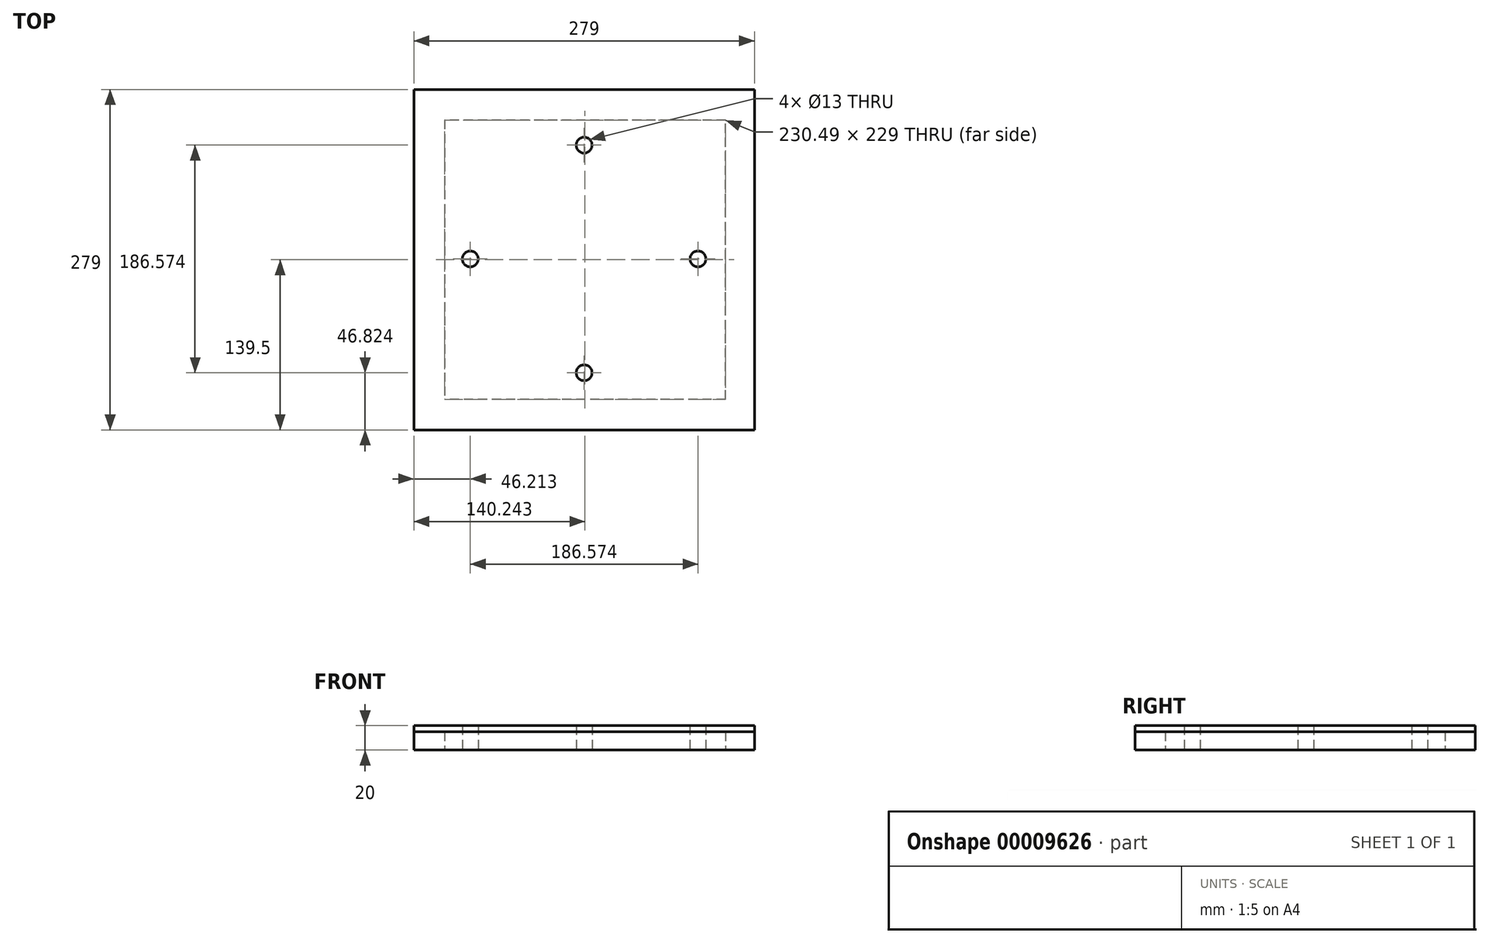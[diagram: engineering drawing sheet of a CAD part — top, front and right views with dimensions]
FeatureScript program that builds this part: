
annotation { "Feature Type Name" : "Feature", "Feature Type Description" : "" }
export const myFeature = defineFeature(function(context is Context, id is Id, definition is map)
    precondition{}
    {
        {
            var Q0;
            Q0=qCreatedBy(makeId("Top.planeOp"),FACE);
            var sketch = newSketch(context, id + "F0", { "sketchPlane" : qUnion([Q0])});
            skLineSegment(sketch, "E0.rect.bottom", {"start": v(89.5, 89.5) * mm, "end": v(-89.5, 89.5) * mm});
            skLineSegment(sketch, "E0.rect.top", {"start": v(89.5, -89.5) * mm, "end": v(-89.5, -89.5) * mm});
            skLineSegment(sketch, "E0.rect.left", {"start": v(89.5, 89.5) * mm, "end": v(89.5, -89.5) * mm});
            skLineSegment(sketch, "E0.rect.right", {"start": v(-89.5, 89.5) * mm, "end": v(-89.5, -89.5) * mm});
            skPoint(sketch, "E0.rect.middle", {"position": v(0, 0) * mm});
            skLineSegment(sketch, "E1.0", {"start": v(115.99, 114.5) * mm, "end": v(-114.5, 114.5) * mm});
            skLineSegment(sketch, "E1.2", {"start": v(115.99, -114.5) * mm, "end": v(-114.5, -114.5) * mm});
            skLineSegment(sketch, "E1.3", {"start": v(-114.5, 114.5) * mm, "end": v(-114.5, -114.5) * mm});
            skLineSegment(sketch, "E2.0", {"start": v(139.5, 139.5) * mm, "end": v(-139.5, 139.5) * mm});
            skLineSegment(sketch, "E2.1", {"start": v(139.5, 139.5) * mm, "end": v(139.5, -139.5) * mm});
            skLineSegment(sketch, "E2.2", {"start": v(139.5, -139.5) * mm, "end": v(-139.5, -139.5) * mm});
            skLineSegment(sketch, "E2.3", {"start": v(-139.5, 139.5) * mm, "end": v(-139.5, -139.5) * mm});
            skLineSegment(sketch, "E3", {"start": v(-3.54, 111.58) * mm, "end": v(-110.96, 4.15) * mm});
            skLineSegment(sketch, "E4", {"start": v(-110.96, -2.92) * mm, "end": v(-3.54, -110.35) * mm});
            skLineSegment(sketch, "E5", {"start": v(3.54, -110.35) * mm, "end": v(110.96, -2.92) * mm});
            skLineSegment(sketch, "E6", {"start": v(110.96, 4.15) * mm, "end": v(3.54, 111.58) * mm});
            skLineSegment(sketch, "E7", {"start": v(57.25, 57.86) * mm, "end": v(-57.25, -56.64) * mm, "construction": true});
            skLineSegment(sketch, "E8", {"start": v(-57.25, 57.86) * mm, "end": v(57.25, -56.64) * mm, "construction": true});
            skPoint(sketch, "E9.visualSharp", {"position": v(0, 115.11) * mm});
            skArc(sketch, "E9.filletArc", {"start": v(3.54, 111.58) * mm, "mid": v(0, 113.04) * mm, "end": v(-3.54, 111.58) * mm});
            skPoint(sketch, "E10.visualSharp", {"position": v(114.5, 0.61) * mm});
            skArc(sketch, "E10.filletArc", {"start": v(110.96, -2.92) * mm, "mid": v(112.43, 0.61) * mm, "end": v(110.96, 4.15) * mm});
            skPoint(sketch, "E11.visualSharp", {"position": v(0, -113.89) * mm});
            skArc(sketch, "E11.filletArc", {"start": v(-3.54, -110.35) * mm, "mid": v(0, -111.82) * mm, "end": v(3.54, -110.35) * mm});
            skPoint(sketch, "E12.visualSharp", {"position": v(-114.5, 0.61) * mm});
            skArc(sketch, "E12.filletArc", {"start": v(-110.96, 4.15) * mm, "mid": v(-112.43, 0.61) * mm, "end": v(-110.96, -2.92) * mm});
            skLineSegment(sketch, "E13", {"start": v(-57.25, 57.86) * mm, "end": v(57.25, 57.86) * mm});
            skLineSegment(sketch, "E14", {"start": v(57.25, 57.86) * mm, "end": v(57.25, -56.64) * mm});
            skLineSegment(sketch, "E15", {"start": v(57.25, -56.64) * mm, "end": v(-57.25, -56.64) * mm});
            skLineSegment(sketch, "E16", {"start": v(-57.25, -56.64) * mm, "end": v(-57.25, 57.86) * mm});
            skLineSegment(sketch, "E17", {"start": v(0, 0) * mm, "end": v(0, -113.89) * mm, "construction": true});
            skPoint(sketch, "E18", {"position": v(0, -92.68) * mm});
            skLineSegment(sketch, "E19", {"start": v(-107.43, 0.61) * mm, "end": v(107.43, 0.61) * mm, "construction": true});
            skLineSegment(sketch, "E20", {"start": v(0, 108.04) * mm, "end": v(0, 0) * mm, "construction": true});
            skPoint(sketch, "E21", {"position": v(-93.29, 0.61) * mm});
            skPoint(sketch, "E22", {"position": v(0, 93.9) * mm});
            skPoint(sketch, "E23", {"position": v(93.29, 0.61) * mm});
            skCircle(sketch, "E24", {"center": v(0, -92.68) * mm, "radius": 6.5 * mm});
            skCircle(sketch, "E25", {"center": v(93.29, 0.61) * mm, "radius": 6.5 * mm});
            skCircle(sketch, "E26", {"center": v(-93.29, 0.61) * mm, "radius": 6.5 * mm});
            skCircle(sketch, "E27", {"center": v(0, 93.9) * mm, "radius": 6.5 * mm});
            skLineSegment(sketch, "E28", {"start": v(115.99, -114.5) * mm, "end": v(115.99, 114.5) * mm});
            skPoint(sketch, "E29.orphan", {"position": v(109.2, 114.5) * mm});
            skSolve(sketch);
        }
        {
            var Q0;
            Q0=makeQuery(id+"F0.imprint","IMPRINT",FACE,{"disambiguationData":[TD([[makeQuery(id+"F0.imprint","IMPRINT",EDGE,{"derivedFrom":sQuery(id+"F0.wireOp",EDGE,"E0.rect.bottom")}),1.0]])]});
            var Q1;
            Q1=makeQuery(id+"F0.imprint","IMPRINT",FACE,{"disambiguationData":[TD([[makeQuery(id+"F0.imprint","IMPRINT",EDGE,{"derivedFrom":sQuery(id+"F0.wireOp",EDGE,"E13")}),-1.0]])]});
            var Q2;
            {var subQ1=sQuery(id+"F0.wireOp",EDGE,"E0.rect.right");var subQ4=sQuery(id+"F0.wireOp",EDGE,"E0.rect.bottom");var subQ6=makeQuery(id+"F0.imprint","INTERSECT",VERTEX,{"derivedFrom":[subQ4,subQ1]});Q2=makeQuery(id+"F0.imprint","IMPRINT",FACE,{"disambiguationData":[TD([[makeQuery(id+"F0.imprint","IMPRINT",EDGE,{"disambiguationData":[TD([[subQ6,1.0]])],"derivedFrom":subQ4}),1.0]])]});}
            var Q3;
            {var subQ4=sQuery(id+"F0.wireOp",EDGE,"E16");Q3=makeQuery(id+"F0.imprint","IMPRINT",FACE,{"disambiguationData":[TD([[makeQuery(id+"F0.imprint","IMPRINT",EDGE,{"derivedFrom":subQ4}),1.0]])]});}
            var Q4;
            {var subQ1=sQuery(id+"F0.wireOp",EDGE,"E0.rect.bottom");var subQ4=sQuery(id+"F0.wireOp",EDGE,"E0.rect.left");var subQ6=makeQuery(id+"F0.imprint","INTERSECT",VERTEX,{"derivedFrom":[subQ1,subQ4]});Q4=makeQuery(id+"F0.imprint","IMPRINT",FACE,{"disambiguationData":[TD([[makeQuery(id+"F0.imprint","IMPRINT",EDGE,{"disambiguationData":[TD([[subQ6,-1.0]])],"derivedFrom":subQ1}),1.0]])]});}
            var Q5;
            {var subQ4=sQuery(id+"F0.wireOp",EDGE,"E14");Q5=makeQuery(id+"F0.imprint","IMPRINT",FACE,{"disambiguationData":[TD([[makeQuery(id+"F0.imprint","IMPRINT",EDGE,{"derivedFrom":subQ4}),1.0]])]});}
            var Q6;
            {var subQ1=sQuery(id+"F0.wireOp",EDGE,"E0.rect.left");var subQ4=sQuery(id+"F0.wireOp",EDGE,"E0.rect.top");var subQ6=makeQuery(id+"F0.imprint","INTERSECT",VERTEX,{"derivedFrom":[subQ4,subQ1]});Q6=makeQuery(id+"F0.imprint","IMPRINT",FACE,{"disambiguationData":[TD([[makeQuery(id+"F0.imprint","IMPRINT",EDGE,{"disambiguationData":[TD([[subQ6,-1.0]])],"derivedFrom":subQ4}),-1.0]])]});}
            var Q7;
            {var subQ4=sQuery(id+"F0.wireOp",EDGE,"E15");Q7=makeQuery(id+"F0.imprint","IMPRINT",FACE,{"disambiguationData":[TD([[makeQuery(id+"F0.imprint","IMPRINT",EDGE,{"derivedFrom":subQ4}),1.0]])]});}
            var Q8;
            {var subQ1=sQuery(id+"F0.wireOp",EDGE,"E0.rect.top");var subQ4=sQuery(id+"F0.wireOp",EDGE,"E0.rect.right");var subQ6=makeQuery(id+"F0.imprint","INTERSECT",VERTEX,{"derivedFrom":[subQ1,subQ4]});Q8=makeQuery(id+"F0.imprint","IMPRINT",FACE,{"disambiguationData":[TD([[makeQuery(id+"F0.imprint","IMPRINT",EDGE,{"disambiguationData":[TD([[subQ6,1.0]])],"derivedFrom":subQ1}),-1.0]])]});}
            var Q9;
            {var subQ0=sQuery(id+"F0.wireOp",EDGE,"E26");var subQ1=sQuery(id+"F0.wireOp",EDGE,"E0.rect.right");var subQ3=makeQuery(id+"F0.imprint","INTERSECT",VERTEX,{"disambiguationData":[OD(0.0)],"derivedFrom":[subQ1,subQ0]});Q9=makeQuery(id+"F0.imprint","IMPRINT",FACE,{"disambiguationData":[TD([[makeQuery(id+"F0.imprint","IMPRINT",EDGE,{"disambiguationData":[TD([[subQ3,-1.0]])],"derivedFrom":subQ1}),1.0]])]});}
            var Q10;
            {var subQ0=sQuery(id+"F0.wireOp",EDGE,"E25");var subQ1=sQuery(id+"F0.wireOp",EDGE,"E0.rect.left");var subQ3=makeQuery(id+"F0.imprint","INTERSECT",VERTEX,{"disambiguationData":[OD(0.0)],"derivedFrom":[subQ1,subQ0]});Q10=makeQuery(id+"F0.imprint","IMPRINT",FACE,{"disambiguationData":[TD([[makeQuery(id+"F0.imprint","IMPRINT",EDGE,{"disambiguationData":[TD([[subQ3,-1.0]])],"derivedFrom":subQ1}),-1.0]])]});}
            var Q11;
            {var subQ0=sQuery(id+"F0.wireOp",EDGE,"E27");var subQ1=sQuery(id+"F0.wireOp",EDGE,"E0.rect.bottom");var subQ3=makeQuery(id+"F0.imprint","INTERSECT",VERTEX,{"disambiguationData":[OD(0.0)],"derivedFrom":[subQ1,subQ0]});Q11=makeQuery(id+"F0.imprint","IMPRINT",FACE,{"disambiguationData":[TD([[makeQuery(id+"F0.imprint","IMPRINT",EDGE,{"disambiguationData":[TD([[subQ3,-1.0]])],"derivedFrom":subQ1}),1.0]])]});}
            var Q12;
            {var subQ0=sQuery(id+"F0.wireOp",EDGE,"E24");var subQ1=sQuery(id+"F0.wireOp",EDGE,"E0.rect.top");var subQ3=makeQuery(id+"F0.imprint","INTERSECT",VERTEX,{"disambiguationData":[OD(0.0)],"derivedFrom":[subQ1,subQ0]});Q12=makeQuery(id+"F0.imprint","IMPRINT",FACE,{"disambiguationData":[TD([[makeQuery(id+"F0.imprint","IMPRINT",EDGE,{"disambiguationData":[TD([[subQ3,-1.0]])],"derivedFrom":subQ1}),-1.0]])]});}
            extrude(context, id + "F1", {"entities" : qUnion([Q0, Q1, Q2, Q3, Q4, Q5, Q6, Q7, Q8, Q9, Q10, Q11, Q12]), "depth" : 15 * mm});
        }
        {
            var Q0;
            {var subQ4=sQuery(id+"F0.wireOp",EDGE,"E12.filletArc");Q0=makeQuery(id+"F0.imprint","IMPRINT",FACE,{"disambiguationData":[TD([[makeQuery(id+"F0.imprint","IMPRINT",EDGE,{"derivedFrom":subQ4}),1.0]])]});}
            var Q1;
            {var subQ3=sQuery(id+"F0.wireOp",EDGE,"E11.filletArc");Q1=makeQuery(id+"F0.imprint","IMPRINT",FACE,{"disambiguationData":[TD([[makeQuery(id+"F0.imprint","IMPRINT",EDGE,{"derivedFrom":subQ3}),1.0]])]});}
            var Q2;
            {var subQ4=sQuery(id+"F0.wireOp",EDGE,"E10.filletArc");Q2=makeQuery(id+"F0.imprint","IMPRINT",FACE,{"disambiguationData":[TD([[makeQuery(id+"F0.imprint","IMPRINT",EDGE,{"derivedFrom":subQ4}),1.0]])]});}
            var Q3;
            {var subQ4=sQuery(id+"F0.wireOp",EDGE,"E9.filletArc");Q3=makeQuery(id+"F0.imprint","IMPRINT",FACE,{"disambiguationData":[TD([[makeQuery(id+"F0.imprint","IMPRINT",EDGE,{"derivedFrom":subQ4}),1.0]])]});}
            var Q4;
            {var subQ0=sQuery(id+"F0.wireOp",EDGE,"E27");var subQ1=sQuery(id+"F0.wireOp",EDGE,"E0.rect.bottom");var subQ3=makeQuery(id+"F0.imprint","INTERSECT",VERTEX,{"disambiguationData":[OD(0.0)],"derivedFrom":[subQ1,subQ0]});Q4=makeQuery(id+"F0.imprint","IMPRINT",FACE,{"disambiguationData":[TD([[makeQuery(id+"F0.imprint","IMPRINT",EDGE,{"disambiguationData":[TD([[subQ3,-1.0]])],"derivedFrom":subQ1}),-1.0]])]});}
            var Q5;
            {var subQ0=sQuery(id+"F0.wireOp",EDGE,"E26");var subQ1=sQuery(id+"F0.wireOp",EDGE,"E0.rect.right");var subQ3=makeQuery(id+"F0.imprint","INTERSECT",VERTEX,{"disambiguationData":[OD(0.0)],"derivedFrom":[subQ1,subQ0]});Q5=makeQuery(id+"F0.imprint","IMPRINT",FACE,{"disambiguationData":[TD([[makeQuery(id+"F0.imprint","IMPRINT",EDGE,{"disambiguationData":[TD([[subQ3,-1.0]])],"derivedFrom":subQ1}),-1.0]])]});}
            var Q6;
            {var subQ0=sQuery(id+"F0.wireOp",EDGE,"E25");var subQ1=sQuery(id+"F0.wireOp",EDGE,"E0.rect.left");var subQ3=makeQuery(id+"F0.imprint","INTERSECT",VERTEX,{"disambiguationData":[OD(0.0)],"derivedFrom":[subQ1,subQ0]});Q6=makeQuery(id+"F0.imprint","IMPRINT",FACE,{"disambiguationData":[TD([[makeQuery(id+"F0.imprint","IMPRINT",EDGE,{"disambiguationData":[TD([[subQ3,-1.0]])],"derivedFrom":subQ1}),1.0]])]});}
            var Q7;
            {var subQ0=sQuery(id+"F0.wireOp",EDGE,"E24");var subQ1=sQuery(id+"F0.wireOp",EDGE,"E0.rect.top");var subQ3=makeQuery(id+"F0.imprint","INTERSECT",VERTEX,{"disambiguationData":[OD(0.0)],"derivedFrom":[subQ1,subQ0]});Q7=makeQuery(id+"F0.imprint","IMPRINT",FACE,{"disambiguationData":[TD([[makeQuery(id+"F0.imprint","IMPRINT",EDGE,{"disambiguationData":[TD([[subQ3,-1.0]])],"derivedFrom":subQ1}),1.0]])]});}
            extrude(context, id + "F2", {"entities" : qUnion([Q0, Q1, Q2, Q3, Q4, Q5, Q6, Q7]), "operationType" : NewBodyOperationType.ADD, "depth" : 15 * mm});
        }
        {
            var Q0;
            Q0=makeQuery(id+"F0.imprint","IMPRINT",FACE,{"disambiguationData":[TD([[makeQuery(id+"F0.imprint","IMPRINT",EDGE,{"derivedFrom":sQuery(id+"F0.wireOp",EDGE,"E1.0")}),-1.0]])]});
            extrude(context, id + "F3", {"entities" : qUnion([Q0]), "depth" : 15 * mm});
        }
        {
            var Q0;
            Q0=makeQuery(id+"F0.imprint","IMPRINT",FACE,{"disambiguationData":[TD([[makeQuery(id+"F0.imprint","IMPRINT",EDGE,{"derivedFrom":sQuery(id+"F0.wireOp",EDGE,"E1.0")}),1.0]])]});
            var Q1;
            Q1=makeQuery(id+"F0.imprint","IMPRINT",FACE,{"disambiguationData":[TD([[makeQuery(id+"F0.imprint","IMPRINT",EDGE,{"derivedFrom":sQuery(id+"F0.wireOp",EDGE,"E1.0")}),-1.0]])]});
            var Q2;
            {var subQ4=sQuery(id+"F0.wireOp",EDGE,"E16");Q2=makeQuery(id+"F0.imprint","IMPRINT",FACE,{"disambiguationData":[TD([[makeQuery(id+"F0.imprint","IMPRINT",EDGE,{"derivedFrom":subQ4}),1.0]])]});}
            var Q3;
            Q3=makeQuery(id+"F0.imprint","IMPRINT",FACE,{"disambiguationData":[TD([[makeQuery(id+"F0.imprint","IMPRINT",EDGE,{"derivedFrom":sQuery(id+"F0.wireOp",EDGE,"E13")}),-1.0]])]});
            var Q4;
            {var subQ1=sQuery(id+"F0.wireOp",EDGE,"E0.rect.right");var subQ4=sQuery(id+"F0.wireOp",EDGE,"E0.rect.bottom");var subQ6=makeQuery(id+"F0.imprint","INTERSECT",VERTEX,{"derivedFrom":[subQ4,subQ1]});Q4=makeQuery(id+"F0.imprint","IMPRINT",FACE,{"disambiguationData":[TD([[makeQuery(id+"F0.imprint","IMPRINT",EDGE,{"disambiguationData":[TD([[subQ6,1.0]])],"derivedFrom":subQ4}),1.0]])]});}
            var Q5;
            {var subQ4=sQuery(id+"F0.wireOp",EDGE,"E12.filletArc");Q5=makeQuery(id+"F0.imprint","IMPRINT",FACE,{"disambiguationData":[TD([[makeQuery(id+"F0.imprint","IMPRINT",EDGE,{"derivedFrom":subQ4}),1.0]])]});}
            var Q6;
            {var subQ1=sQuery(id+"F0.wireOp",EDGE,"E0.rect.bottom");var subQ4=sQuery(id+"F0.wireOp",EDGE,"E0.rect.left");var subQ6=makeQuery(id+"F0.imprint","INTERSECT",VERTEX,{"derivedFrom":[subQ1,subQ4]});Q6=makeQuery(id+"F0.imprint","IMPRINT",FACE,{"disambiguationData":[TD([[makeQuery(id+"F0.imprint","IMPRINT",EDGE,{"disambiguationData":[TD([[subQ6,-1.0]])],"derivedFrom":subQ1}),1.0]])]});}
            var Q7;
            {var subQ4=sQuery(id+"F0.wireOp",EDGE,"E9.filletArc");Q7=makeQuery(id+"F0.imprint","IMPRINT",FACE,{"disambiguationData":[TD([[makeQuery(id+"F0.imprint","IMPRINT",EDGE,{"derivedFrom":subQ4}),1.0]])]});}
            var Q8;
            {var subQ0=sQuery(id+"F0.wireOp",EDGE,"E27");var subQ1=sQuery(id+"F0.wireOp",EDGE,"E0.rect.bottom");var subQ3=makeQuery(id+"F0.imprint","INTERSECT",VERTEX,{"disambiguationData":[OD(0.0)],"derivedFrom":[subQ1,subQ0]});Q8=makeQuery(id+"F0.imprint","IMPRINT",FACE,{"disambiguationData":[TD([[makeQuery(id+"F0.imprint","IMPRINT",EDGE,{"disambiguationData":[TD([[subQ3,-1.0]])],"derivedFrom":subQ1}),-1.0]])]});}
            var Q9;
            {var subQ4=sQuery(id+"F0.wireOp",EDGE,"E13");Q9=makeQuery(id+"F0.imprint","IMPRINT",FACE,{"disambiguationData":[TD([[makeQuery(id+"F0.imprint","IMPRINT",EDGE,{"derivedFrom":subQ4}),1.0]])]});}
            var Q10;
            {var subQ1=sQuery(id+"F0.wireOp",EDGE,"E0.rect.top");var subQ4=sQuery(id+"F0.wireOp",EDGE,"E0.rect.right");var subQ6=makeQuery(id+"F0.imprint","INTERSECT",VERTEX,{"derivedFrom":[subQ1,subQ4]});Q10=makeQuery(id+"F0.imprint","IMPRINT",FACE,{"disambiguationData":[TD([[makeQuery(id+"F0.imprint","IMPRINT",EDGE,{"disambiguationData":[TD([[subQ6,1.0]])],"derivedFrom":subQ1}),-1.0]])]});}
            var Q11;
            {var subQ4=sQuery(id+"F0.wireOp",EDGE,"E15");Q11=makeQuery(id+"F0.imprint","IMPRINT",FACE,{"disambiguationData":[TD([[makeQuery(id+"F0.imprint","IMPRINT",EDGE,{"derivedFrom":subQ4}),1.0]])]});}
            var Q12;
            {var subQ0=sQuery(id+"F0.wireOp",EDGE,"E14");Q12=makeQuery(id+"F0.imprint","IMPRINT",FACE,{"disambiguationData":[TD([[makeQuery(id+"F0.imprint","IMPRINT",EDGE,{"derivedFrom":subQ0}),1.0]])]});}
            var Q13;
            {var subQ4=sQuery(id+"F0.wireOp",EDGE,"E10.filletArc");Q13=makeQuery(id+"F0.imprint","IMPRINT",FACE,{"disambiguationData":[TD([[makeQuery(id+"F0.imprint","IMPRINT",EDGE,{"derivedFrom":subQ4}),1.0]])]});}
            var Q14;
            {var subQ0=sQuery(id+"F0.wireOp",EDGE,"E25");var subQ1=sQuery(id+"F0.wireOp",EDGE,"E0.rect.left");var subQ3=makeQuery(id+"F0.imprint","INTERSECT",VERTEX,{"disambiguationData":[OD(0.0)],"derivedFrom":[subQ1,subQ0]});Q14=makeQuery(id+"F0.imprint","IMPRINT",FACE,{"disambiguationData":[TD([[makeQuery(id+"F0.imprint","IMPRINT",EDGE,{"disambiguationData":[TD([[subQ3,-1.0]])],"derivedFrom":subQ1}),1.0]])]});}
            var Q15;
            {var subQ0=sQuery(id+"F0.wireOp",EDGE,"E26");var subQ1=sQuery(id+"F0.wireOp",EDGE,"E0.rect.right");var subQ3=makeQuery(id+"F0.imprint","INTERSECT",VERTEX,{"disambiguationData":[OD(0.0)],"derivedFrom":[subQ1,subQ0]});Q15=makeQuery(id+"F0.imprint","IMPRINT",FACE,{"disambiguationData":[TD([[makeQuery(id+"F0.imprint","IMPRINT",EDGE,{"disambiguationData":[TD([[subQ3,-1.0]])],"derivedFrom":subQ1}),-1.0]])]});}
            var Q16;
            {var subQ1=sQuery(id+"F0.wireOp",EDGE,"E0.rect.left");var subQ4=sQuery(id+"F0.wireOp",EDGE,"E0.rect.top");var subQ6=makeQuery(id+"F0.imprint","INTERSECT",VERTEX,{"derivedFrom":[subQ4,subQ1]});Q16=makeQuery(id+"F0.imprint","IMPRINT",FACE,{"disambiguationData":[TD([[makeQuery(id+"F0.imprint","IMPRINT",EDGE,{"disambiguationData":[TD([[subQ6,-1.0]])],"derivedFrom":subQ4}),-1.0]])]});}
            var Q17;
            {var subQ0=sQuery(id+"F0.wireOp",EDGE,"E24");var subQ1=sQuery(id+"F0.wireOp",EDGE,"E0.rect.top");var subQ3=makeQuery(id+"F0.imprint","INTERSECT",VERTEX,{"disambiguationData":[OD(0.0)],"derivedFrom":[subQ1,subQ0]});Q17=makeQuery(id+"F0.imprint","IMPRINT",FACE,{"disambiguationData":[TD([[makeQuery(id+"F0.imprint","IMPRINT",EDGE,{"disambiguationData":[TD([[subQ3,-1.0]])],"derivedFrom":subQ1}),1.0]])]});}
            var Q18;
            {var subQ4=sQuery(id+"F0.wireOp",EDGE,"E11.filletArc");Q18=makeQuery(id+"F0.imprint","IMPRINT",FACE,{"disambiguationData":[TD([[makeQuery(id+"F0.imprint","IMPRINT",EDGE,{"derivedFrom":subQ4}),1.0]])]});}
            var Q19;
            {var subQ0=sQuery(id+"F0.wireOp",EDGE,"E24");var subQ1=sQuery(id+"F0.wireOp",EDGE,"E0.rect.top");var subQ3=makeQuery(id+"F0.imprint","INTERSECT",VERTEX,{"disambiguationData":[OD(0.0)],"derivedFrom":[subQ1,subQ0]});Q19=makeQuery(id+"F0.imprint","IMPRINT",FACE,{"disambiguationData":[TD([[makeQuery(id+"F0.imprint","IMPRINT",EDGE,{"disambiguationData":[TD([[subQ3,-1.0]])],"derivedFrom":subQ1}),-1.0]])]});}
            var Q20;
            {var subQ0=sQuery(id+"F0.wireOp",EDGE,"E25");var subQ1=sQuery(id+"F0.wireOp",EDGE,"E0.rect.left");var subQ3=makeQuery(id+"F0.imprint","INTERSECT",VERTEX,{"disambiguationData":[OD(0.0)],"derivedFrom":[subQ1,subQ0]});Q20=makeQuery(id+"F0.imprint","IMPRINT",FACE,{"disambiguationData":[TD([[makeQuery(id+"F0.imprint","IMPRINT",EDGE,{"disambiguationData":[TD([[subQ3,-1.0]])],"derivedFrom":subQ1}),-1.0]])]});}
            var Q21;
            {var subQ0=sQuery(id+"F0.wireOp",EDGE,"E27");var subQ1=sQuery(id+"F0.wireOp",EDGE,"E0.rect.bottom");var subQ3=makeQuery(id+"F0.imprint","INTERSECT",VERTEX,{"disambiguationData":[OD(0.0)],"derivedFrom":[subQ1,subQ0]});Q21=makeQuery(id+"F0.imprint","IMPRINT",FACE,{"disambiguationData":[TD([[makeQuery(id+"F0.imprint","IMPRINT",EDGE,{"disambiguationData":[TD([[subQ3,-1.0]])],"derivedFrom":subQ1}),1.0]])]});}
            var Q22;
            {var subQ0=sQuery(id+"F0.wireOp",EDGE,"E26");var subQ1=sQuery(id+"F0.wireOp",EDGE,"E0.rect.right");var subQ3=makeQuery(id+"F0.imprint","INTERSECT",VERTEX,{"disambiguationData":[OD(0.0)],"derivedFrom":[subQ1,subQ0]});Q22=makeQuery(id+"F0.imprint","IMPRINT",FACE,{"disambiguationData":[TD([[makeQuery(id+"F0.imprint","IMPRINT",EDGE,{"disambiguationData":[TD([[subQ3,-1.0]])],"derivedFrom":subQ1}),1.0]])]});}
            extrude(context, id + "F4", {"entities" : qUnion([Q0, Q1, Q2, Q3, Q4, Q5, Q6, Q7, Q8, Q9, Q10, Q11, Q12, Q13, Q14, Q15, Q16, Q17, Q18, Q19, Q20, Q21, Q22]), "depth" : 20 * mm});
        }
        {
            var Q0;
            Q0=makeQuery(id+"F0.imprint","IMPRINT",FACE,{"disambiguationData":[TD([[makeQuery(id+"F0.imprint","IMPRINT",EDGE,{"derivedFrom":sQuery(id+"F0.wireOp",EDGE,"E1.0")}),1.0]])]});
            extrude(context, id + "F5", {"entities" : qUnion([Q0]), "depth" : 15 * mm});
        }
        {
            var Q0;
            {var subQ4=sQuery(id+"F0.wireOp",EDGE,"E12.filletArc");Q0=makeQuery(id+"F0.imprint","IMPRINT",FACE,{"disambiguationData":[TD([[makeQuery(id+"F0.imprint","IMPRINT",EDGE,{"derivedFrom":subQ4}),1.0]])]});}
            var Q1;
            {var subQ4=sQuery(id+"F0.wireOp",EDGE,"E9.filletArc");Q1=makeQuery(id+"F0.imprint","IMPRINT",FACE,{"disambiguationData":[TD([[makeQuery(id+"F0.imprint","IMPRINT",EDGE,{"derivedFrom":subQ4}),1.0]])]});}
            var Q2;
            {var subQ4=sQuery(id+"F0.wireOp",EDGE,"E10.filletArc");Q2=makeQuery(id+"F0.imprint","IMPRINT",FACE,{"disambiguationData":[TD([[makeQuery(id+"F0.imprint","IMPRINT",EDGE,{"derivedFrom":subQ4}),1.0]])]});}
            var Q3;
            {var subQ4=sQuery(id+"F0.wireOp",EDGE,"E11.filletArc");Q3=makeQuery(id+"F0.imprint","IMPRINT",FACE,{"disambiguationData":[TD([[makeQuery(id+"F0.imprint","IMPRINT",EDGE,{"derivedFrom":subQ4}),1.0]])]});}
            var Q4;
            {var subQ0=sQuery(id+"F0.wireOp",EDGE,"E24");var subQ1=sQuery(id+"F0.wireOp",EDGE,"E0.rect.top");var subQ3=makeQuery(id+"F0.imprint","INTERSECT",VERTEX,{"disambiguationData":[OD(0.0)],"derivedFrom":[subQ1,subQ0]});Q4=makeQuery(id+"F0.imprint","IMPRINT",FACE,{"disambiguationData":[TD([[makeQuery(id+"F0.imprint","IMPRINT",EDGE,{"disambiguationData":[TD([[subQ3,-1.0]])],"derivedFrom":subQ1}),1.0]])]});}
            var Q5;
            {var subQ0=sQuery(id+"F0.wireOp",EDGE,"E25");var subQ1=sQuery(id+"F0.wireOp",EDGE,"E0.rect.left");var subQ3=makeQuery(id+"F0.imprint","INTERSECT",VERTEX,{"disambiguationData":[OD(0.0)],"derivedFrom":[subQ1,subQ0]});Q5=makeQuery(id+"F0.imprint","IMPRINT",FACE,{"disambiguationData":[TD([[makeQuery(id+"F0.imprint","IMPRINT",EDGE,{"disambiguationData":[TD([[subQ3,-1.0]])],"derivedFrom":subQ1}),1.0]])]});}
            var Q6;
            {var subQ0=sQuery(id+"F0.wireOp",EDGE,"E26");var subQ1=sQuery(id+"F0.wireOp",EDGE,"E0.rect.right");var subQ3=makeQuery(id+"F0.imprint","INTERSECT",VERTEX,{"disambiguationData":[OD(0.0)],"derivedFrom":[subQ1,subQ0]});Q6=makeQuery(id+"F0.imprint","IMPRINT",FACE,{"disambiguationData":[TD([[makeQuery(id+"F0.imprint","IMPRINT",EDGE,{"disambiguationData":[TD([[subQ3,-1.0]])],"derivedFrom":subQ1}),-1.0]])]});}
            var Q7;
            {var subQ0=sQuery(id+"F0.wireOp",EDGE,"E27");var subQ1=sQuery(id+"F0.wireOp",EDGE,"E0.rect.bottom");var subQ3=makeQuery(id+"F0.imprint","INTERSECT",VERTEX,{"disambiguationData":[OD(0.0)],"derivedFrom":[subQ1,subQ0]});Q7=makeQuery(id+"F0.imprint","IMPRINT",FACE,{"disambiguationData":[TD([[makeQuery(id+"F0.imprint","IMPRINT",EDGE,{"disambiguationData":[TD([[subQ3,-1.0]])],"derivedFrom":subQ1}),-1.0]])]});}
            extrude(context, id + "F6", {"entities" : qUnion([Q0, Q1, Q2, Q3, Q4, Q5, Q6, Q7]), "operationType" : NewBodyOperationType.ADD, "depth" : 10 * mm});
        }
    });
